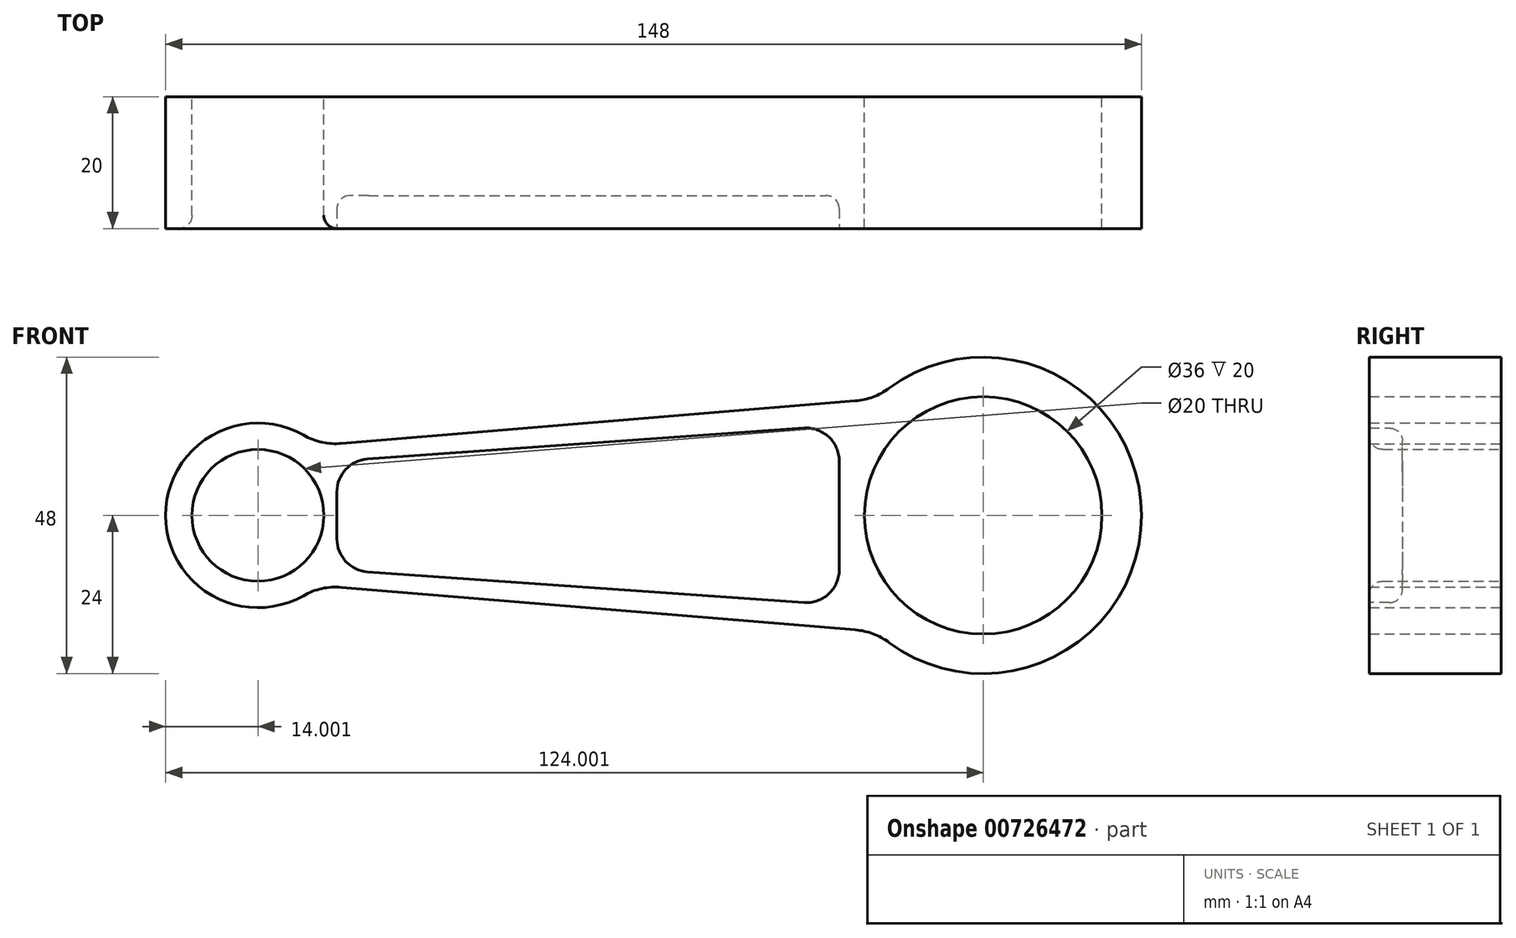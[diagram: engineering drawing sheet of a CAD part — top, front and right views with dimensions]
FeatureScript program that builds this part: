
annotation { "Feature Type Name" : "Feature", "Feature Type Description" : "" }
export const myFeature = defineFeature(function(context is Context, id is Id, definition is map)
    precondition{}
    {
        {
            var Q0;
            Q0=qCreatedBy(makeId("Front.planeOp"),FACE);
            var sketch = newSketch(context, id + "F0", { "sketchPlane" : qUnion([Q0])});
            skCircle(sketch, "E0", {"center": v(-45.33, 0) * mm, "radius": 10 * mm});
            skCircle(sketch, "E1", {"center": v(-45.33, 0) * mm, "radius": 14 * mm});
            skLineSegment(sketch, "E2", {"start": v(-45.33, 0) * mm, "end": v(64.67, 0) * mm});
            skCircle(sketch, "E3", {"center": v(64.67, 0) * mm, "radius": 18 * mm});
            skCircle(sketch, "E4", {"center": v(64.67, 0) * mm, "radius": 24 * mm});
            skLineSegment(sketch, "E5", {"start": v(-36.2, 10.6) * mm, "end": v(48.38, 17.62) * mm});
            skLineSegment(sketch, "E6.MirrorCS", {"start": v(-36.2, -10.6) * mm, "end": v(48.38, -17.62) * mm});
            skSolve(sketch);
        }
        {
            var Q0;
            {var subQ0=sQuery(id+"F0.wireOp",EDGE,"E5");Q0=makeQuery(id+"F0.imprint","IMPRINT",FACE,{"disambiguationData":[TD([[makeQuery(id+"F0.imprint","IMPRINT",EDGE,{"derivedFrom":subQ0}),-1.0]])]});}
            var Q1;
            {var subQ0=sQuery(id+"F0.wireOp",EDGE,"E6.MirrorCS");Q1=makeQuery(id+"F0.imprint","IMPRINT",FACE,{"disambiguationData":[TD([[makeQuery(id+"F0.imprint","IMPRINT",EDGE,{"derivedFrom":subQ0}),1.0]])]});}
            var Q2;
            Q2=makeQuery(id+"F0.imprint","IMPRINT",FACE,{"disambiguationData":[TD([[makeQuery(id+"F0.imprint","IMPRINT",EDGE,{"derivedFrom":sQuery(id+"F0.wireOp",EDGE,"E3")}),-1.0]])]});
            var Q3;
            Q3=makeQuery(id+"F0.imprint","IMPRINT",FACE,{"disambiguationData":[TD([[makeQuery(id+"F0.imprint","IMPRINT",EDGE,{"derivedFrom":sQuery(id+"F0.wireOp",EDGE,"E0")}),-1.0]])]});
            extrude(context, id + "F1", {"entities" : qUnion([Q0, Q1, Q2, Q3]), "endBound" : BoundingType.SYMMETRIC, "depth" : 20 * mm, "offsetDistance" : 25 * mm});
        }
        {
            var Q0;
            Q0=makeQuery(id+"F1.opExtrude","SWEPT_EDGE",EDGE,{"disambiguationData":[OSD([sQuery(id+"F0.wireOp",EDGE,"E1"),sQuery(id+"F0.wireOp",EDGE,"E5")])]});
            fillet(context, id + "F2", {"entities" : qUnion([Q0]), "radius" : 10 * mm, "tangentPropagation" : true, "allowEdgeOverflow" : false});
        }
        {
            var Q0;
            Q0=makeQuery(id+"F1.opExtrude","SWEPT_EDGE",EDGE,{"disambiguationData":[OSD([sQuery(id+"F0.wireOp",EDGE,"E4"),sQuery(id+"F0.wireOp",EDGE,"E5")])]});
            var Q1;
            Q1=makeQuery(id+"F1.opExtrude","SWEPT_EDGE",EDGE,{"disambiguationData":[OSD([sQuery(id+"F0.wireOp",EDGE,"E4"),sQuery(id+"F0.wireOp",EDGE,"E6.MirrorCS")])]});
            var Q2;
            Q2=makeQuery(id+"F1.opExtrude","SWEPT_EDGE",EDGE,{"disambiguationData":[OSD([sQuery(id+"F0.wireOp",EDGE,"E1"),sQuery(id+"F0.wireOp",EDGE,"E6.MirrorCS")])]});
            fillet(context, id + "F3", {"entities" : qUnion([Q0, Q1, Q2]), "radius" : 10 * mm, "tangentPropagation" : true, "allowEdgeOverflow" : false});
        }
        {
            var Q0;
            Q0=makeQuery(id+"F1.opExtrude","CAP_FACE",FACE,{"disambiguationData":[OSD([sQuery(id+"F0.wireOp",EDGE,"E0"),sQuery(id+"F0.wireOp",EDGE,"E1"),sQuery(id+"F0.wireOp",EDGE,"E3"),sQuery(id+"F0.wireOp",EDGE,"E4"),sQuery(id+"F0.wireOp",EDGE,"E5"),sQuery(id+"F0.wireOp",EDGE,"E6.MirrorCS")])],"isStart":false});
            var sketch = newSketch(context, id + "F4", { "sketchPlane" : qUnion([Q0])});
            skLineSegment(sketch, "E7", {"start": v(-33.35, 8.23) * mm, "end": v(-33.35, -8.23) * mm});
            skLineSegment(sketch, "E8", {"start": v(-33.35, 8.23) * mm, "end": v(42.83, 13.61) * mm});
            skLineSegment(sketch, "E9", {"start": v(42.83, 13.61) * mm, "end": v(42.83, -13.61) * mm});
            skLineSegment(sketch, "E10.MirrorCS", {"start": v(-33.35, -8.23) * mm, "end": v(42.83, -13.61) * mm});
            skSolve(sketch);
        }
        {
            var Q0;
            Q0=makeQuery(id+"F4.imprint","IMPRINT",FACE,{"disambiguationData":[TD([[makeQuery(id+"F4.imprint","IMPRINT",EDGE,{"derivedFrom":sQuery(id+"F4.wireOp",EDGE,"E7")}),1.0]])]});
            extrude(context, id + "F5", {"entities" : qUnion([Q0]), "operationType" : NewBodyOperationType.REMOVE, "oppositeDirection" : true, "depth" : 5 * mm, "offsetDistance" : 25 * mm});
        }
        {
            var Q0;
            Q0=makeQuery(id+"F5.boolean.opBoolean","COPY",EDGE,{"derivedFrom":makeQuery(id+"F5.opExtrude","SWEPT_EDGE",EDGE,{"disambiguationData":[OSD([sQuery(id+"F4.wireOp",EDGE,"E7"),sQuery(id+"F4.wireOp",EDGE,"E8")])]})});
            var Q1;
            Q1=makeQuery(id+"F5.boolean.opBoolean","COPY",EDGE,{"derivedFrom":makeQuery(id+"F5.opExtrude","SWEPT_EDGE",EDGE,{"disambiguationData":[OSD([sQuery(id+"F4.wireOp",EDGE,"E7"),sQuery(id+"F4.wireOp",EDGE,"E10.MirrorCS")])]})});
            fillet(context, id + "F6", {"entities" : qUnion([Q0, Q1]), "radius" : 5 * mm, "tangentPropagation" : true, "allowEdgeOverflow" : false});
        }
        {
            var Q0;
            Q0=makeQuery(id+"F5.boolean.opBoolean","COPY",EDGE,{"derivedFrom":makeQuery(id+"F5.opExtrude","SWEPT_EDGE",EDGE,{"disambiguationData":[OSD([sQuery(id+"F4.wireOp",EDGE,"E8"),sQuery(id+"F4.wireOp",EDGE,"E9")])]})});
            var Q1;
            Q1=makeQuery(id+"F5.boolean.opBoolean","COPY",EDGE,{"derivedFrom":makeQuery(id+"F5.opExtrude","SWEPT_EDGE",EDGE,{"disambiguationData":[OSD([sQuery(id+"F4.wireOp",EDGE,"E9"),sQuery(id+"F4.wireOp",EDGE,"E10.MirrorCS")])]})});
            fillet(context, id + "F7", {"entities" : qUnion([Q0, Q1]), "radius" : 5 * mm, "tangentPropagation" : true, "allowEdgeOverflow" : false});
        }
        {
            var Q0;
            Q0=makeQuery(id+"F5.boolean.opBoolean","COPY",EDGE,{"derivedFrom":makeQuery(id+"F5.opExtrude","CAP_EDGE",EDGE,{"disambiguationData":[OSD([sQuery(id+"F4.wireOp",EDGE,"E8")])],"isStart":false})});
            var Q1;
            Q1=makeQuery(id+"F1.opExtrude","CAP_EDGE",EDGE,{"disambiguationData":[OSD([sQuery(id+"F0.wireOp",EDGE,"E0")])],"isStart":false});
            fillet(context, id + "F8", {"entities" : qUnion([Q0, Q1]), "radius" : 2 * mm, "tangentPropagation" : true, "allowEdgeOverflow" : false});
        }
    });
